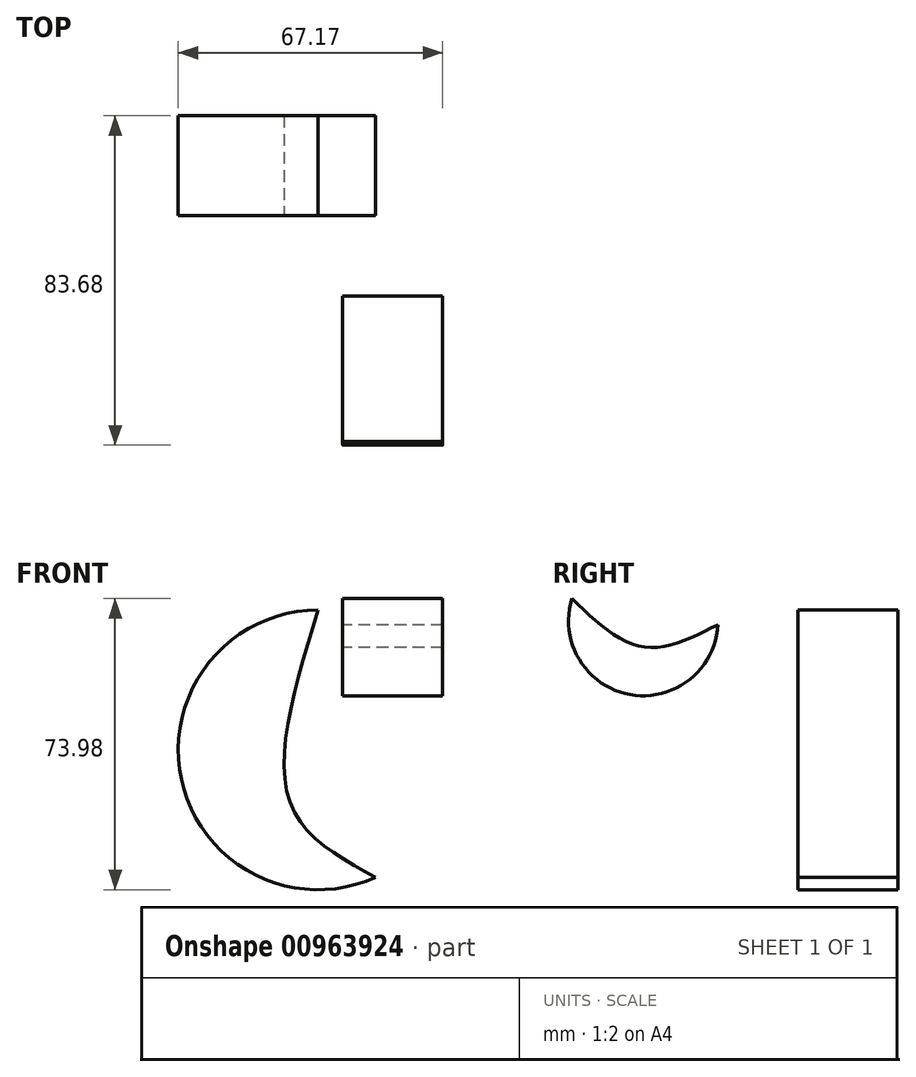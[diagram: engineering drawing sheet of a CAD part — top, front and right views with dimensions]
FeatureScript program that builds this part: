
annotation { "Feature Type Name" : "Feature", "Feature Type Description" : "" }
export const myFeature = defineFeature(function(context is Context, id is Id, definition is map)
    precondition{}
    {
        {
            var Q0;
            Q0=qCreatedBy(makeId("Front.planeOp"),FACE);
            var sketch = newSketch(context, id + "F0", { "sketchPlane" : qUnion([Q0])});
            skArc(sketch, "E0", {"start": v(-6.24, 48.88) * mm, "mid": v(-40.97, 5.87) * mm, "end": v(8.38, -19.05) * mm});
            skFitSpline(sketch, "E1", {"points": [v(-6.24, 48.88) * mm, v(-13.36, 0) * mm, v(8.38, -19.05) * mm], "startDerivative": vector(-30.35, -98.25) * mm, "endDerivative": vector(63.74, -34.74) * mm});
            skSolve(sketch);
        }
        {
            var Q0;
            Q0 = qSketchRegion(id + "F0", true);
            extrude(context, id + "F1", {"entities" : qUnion([Q0]), "depth" : 25.4 * mm, "offsetDistance" : 25.4 * mm});
        }
        {
            var Q0;
            Q0=qCreatedBy(makeId("Right.planeOp"),FACE);
            var sketch = newSketch(context, id + "F2", { "sketchPlane" : qUnion([Q0])});
            skArc(sketch, "E2", {"start": v(-82.8, 51.8) * mm, "mid": v(-68.06, 27.4) * mm, "end": v(-45.77, 45.15) * mm});
            skFitSpline(sketch, "E3", {"points": [v(-45.77, 45.15) * mm, v(-64.71, 39.52) * mm, v(-82.8, 51.8) * mm], "startDerivative": vector(-39.74, -20.2) * mm, "endDerivative": vector(-34.36, 33.03) * mm});
            skSolve(sketch);
        }
        {
            var Q0;
            Q0 = qSketchRegion(id + "F2", true);
            extrude(context, id + "F3", {"entities" : qUnion([Q0]), "depth" : 25.4 * mm, "offsetDistance" : 25.4 * mm});
        }
    });
